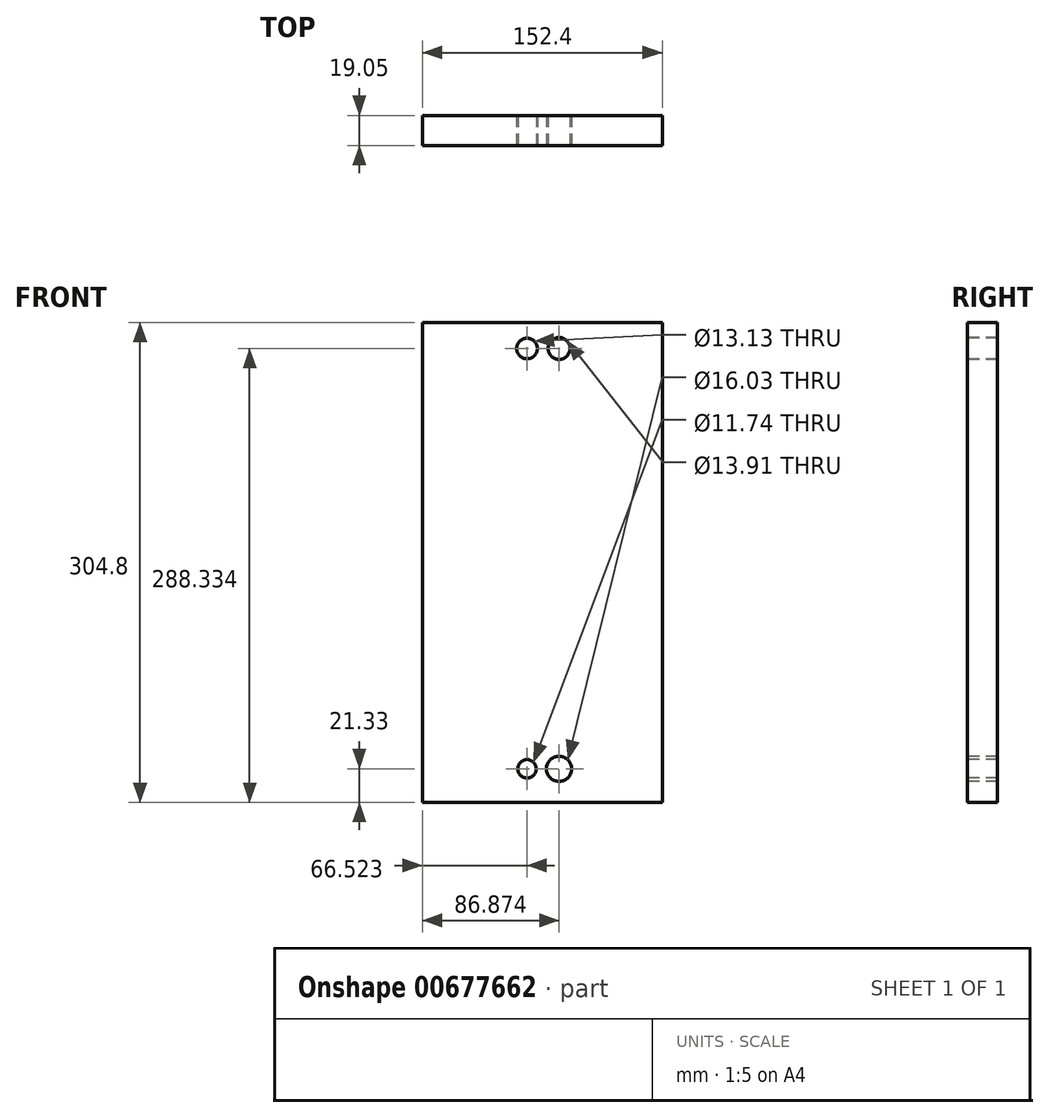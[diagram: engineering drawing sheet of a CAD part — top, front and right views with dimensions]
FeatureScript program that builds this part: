
annotation { "Feature Type Name" : "Feature", "Feature Type Description" : "" }
export const myFeature = defineFeature(function(context is Context, id is Id, definition is map)
    precondition{}
    {
        {
            var Q0;
            Q0=qCreatedBy(makeId("Front.planeOp"),FACE);
            var sketch = newSketch(context, id + "F0", { "sketchPlane" : qUnion([Q0])});
            skLineSegment(sketch, "E0.bottom", {"start": v(0, 0) * mm, "end": v(152.4, 0) * mm});
            skLineSegment(sketch, "E0.top", {"start": v(0, 304.8) * mm, "end": v(152.4, 304.8) * mm});
            skLineSegment(sketch, "E0.left", {"start": v(0, 0) * mm, "end": v(0, 304.8) * mm});
            skLineSegment(sketch, "E0.right", {"start": v(152.4, 0) * mm, "end": v(152.4, 304.8) * mm});
            skSolve(sketch);
        }
        {
            var Q0;
            Q0 = qSketchRegion(id + "F0", true);
            extrude(context, id + "F1", {"entities" : qUnion([Q0]), "oppositeDirection" : true, "depth" : 19.05 * mm, "offsetDistance" : 25.4 * mm});
        }
        {
            var Q0;
            Q0=makeQuery(id+"F1.opExtrude","CAP_FACE",FACE,{"disambiguationData":[OSD([sQuery(id+"F0.wireOp",EDGE,"E0.bottom"),sQuery(id+"F0.wireOp",EDGE,"E0.top"),sQuery(id+"F0.wireOp",EDGE,"E0.left"),sQuery(id+"F0.wireOp",EDGE,"E0.right")])],"isStart":true});
            var sketch = newSketch(context, id + "F2", { "sketchPlane" : qUnion([Q0])});
            skCircle(sketch, "E1", {"center": v(66.52, 288.33) * mm, "radius": 6.56 * mm});
            skCircle(sketch, "E2", {"center": v(86.87, 288.33) * mm, "radius": 6.96 * mm});
            skCircle(sketch, "E3", {"center": v(66.52, 21.33) * mm, "radius": 5.87 * mm});
            skCircle(sketch, "E4", {"center": v(86.87, 21.33) * mm, "radius": 8.02 * mm});
            skSolve(sketch);
        }
        {
            var Q0;
            Q0 = qSketchRegion(id + "F2", true);
            extrude(context, id + "F3", {"entities" : qUnion([Q0]), "operationType" : NewBodyOperationType.REMOVE, "oppositeDirection" : true, "depth" : 25.4 * mm, "offsetDistance" : 25.4 * mm});
        }
    });
